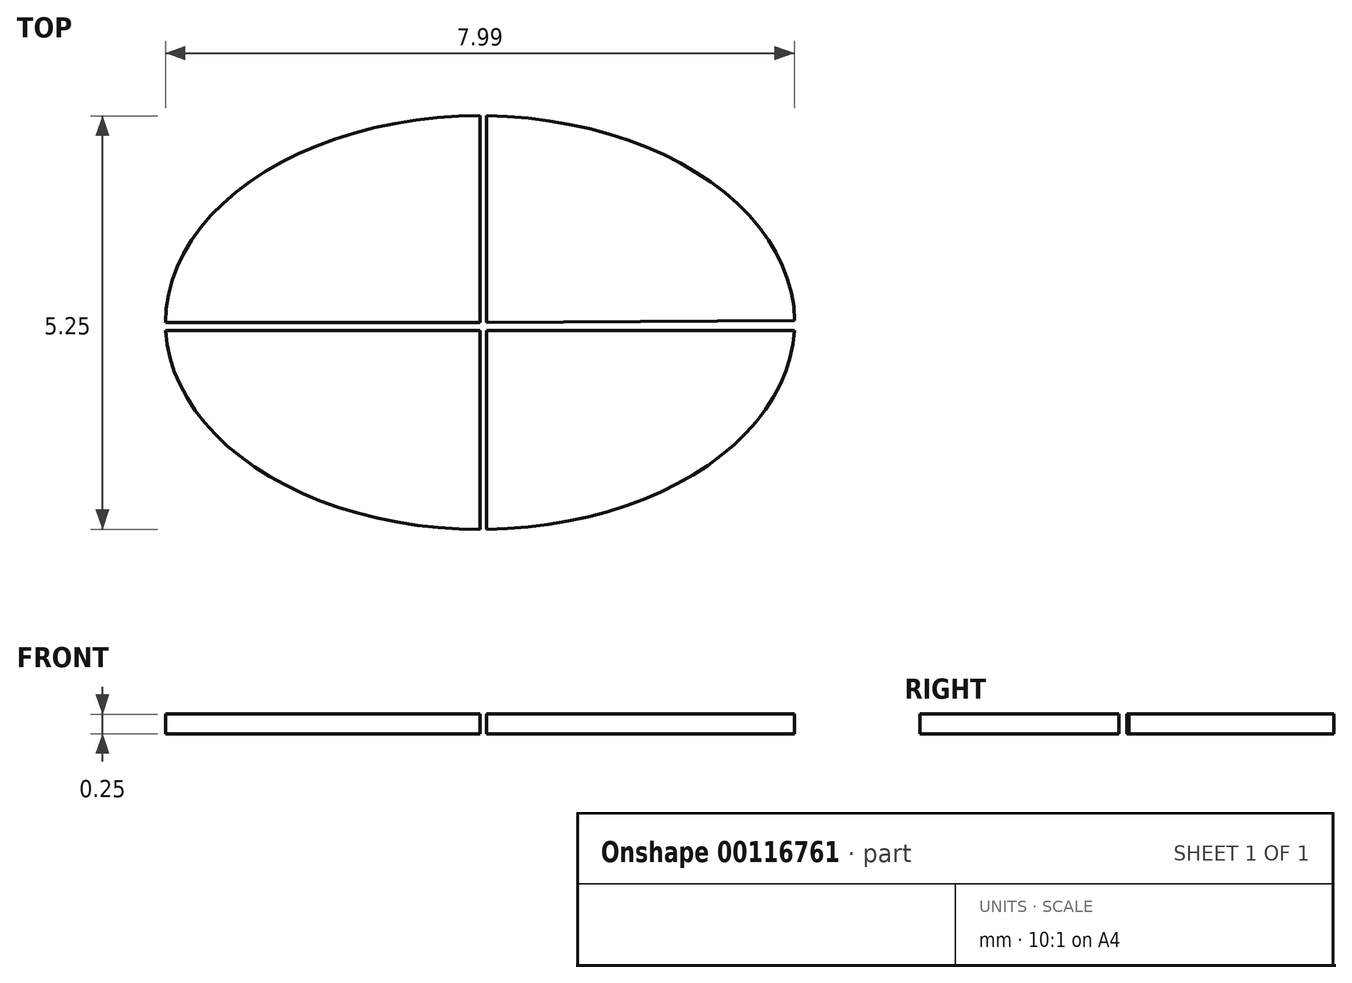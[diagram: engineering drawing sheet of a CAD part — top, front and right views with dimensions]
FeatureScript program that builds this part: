
annotation { "Feature Type Name" : "Feature", "Feature Type Description" : "" }
export const myFeature = defineFeature(function(context is Context, id is Id, definition is map)
    precondition{}
    {
        {
            var Q0;
            Q0=qCreatedBy(makeId("Top.planeOp"),FACE);
            var sketch = newSketch(context, id + "F0", { "sketchPlane" : qUnion([Q0])});
            skEllipticalArc(sketch, "E0", {});
            skLineSegment(sketch, "E1", {"start": v(-42.17, 8.75) * mm, "end": v(-42.17, 11.37) * mm});
            skLineSegment(sketch, "E2", {"start": v(-42.17, 12) * mm, "end": v(-42.09, 12) * mm});
            skLineSegment(sketch, "E3", {"start": v(-42.09, 12) * mm, "end": v(-42.09, 11.51) * mm});
            skLineSegment(sketch, "E4", {"start": v(-42.09, 5.27) * mm, "end": v(-42.17, 5.27) * mm});
            skLineSegment(sketch, "E5", {"start": v(-42.17, 5.27) * mm, "end": v(-42.17, 5.98) * mm});
            skLineSegment(sketch, "E6", {"start": v(-42.17, 8.75) * mm, "end": v(-46.17, 8.75) * mm});
            skLineSegment(sketch, "E7", {"start": v(-47.34, 8.75) * mm, "end": v(-46.3, 8.64) * mm});
            skLineSegment(sketch, "E8", {"start": v(-46.17, 8.64) * mm, "end": v(-42.17, 8.64) * mm});
            skLineSegment(sketch, "E9", {"start": v(-42.09, 8.75) * mm, "end": v(-38.18, 8.77) * mm});
            skLineSegment(sketch, "E10", {"start": v(-38.04, 8.64) * mm, "end": v(-36.9, 8.78) * mm});
            skLineSegment(sketch, "E11.trimOffspring", {"start": v(-42.09, 11.37) * mm, "end": v(-42.09, 8.75) * mm});
            skLineSegment(sketch, "E12.trimOffspring", {"start": v(-42.17, 11.51) * mm, "end": v(-42.17, 12) * mm});
            skLineSegment(sketch, "E13.trimOffspring", {"start": v(-42.09, 8.64) * mm, "end": v(-38.18, 8.64) * mm});
            skLineSegment(sketch, "E14.trimOffspring", {"start": v(-42.09, 8.64) * mm, "end": v(-42.09, 6.12) * mm});
            skEllipticalArc(sketch, "E15.trimOffspring", {});
            skLineSegment(sketch, "E16.trimOffspring", {"start": v(-38.04, 8.77) * mm, "end": v(-36.9, 8.78) * mm});
            skEllipticalArc(sketch, "E17.trimOffspring", {});
            skLineSegment(sketch, "E18.trimOffspring", {"start": v(-42.09, 5.98) * mm, "end": v(-42.09, 5.27) * mm});
            skLineSegment(sketch, "E19.trimOffspring", {"start": v(-42.17, 6.12) * mm, "end": v(-42.17, 8.64) * mm});
            skEllipticalArc(sketch, "E20.trimOffspring", {});
            skEllipticalArc(sketch, "E21.trimOffspring", {});
            skLineSegment(sketch, "E22.trimOffspring", {"start": v(-46.3, 8.75) * mm, "end": v(-47.34, 8.75) * mm});
            const initialGuessF0  = {"E0": [-0.04217269644141197, 0.008745238929242791, 1, 0, 0.004132768626864048, 0.002768394281422402, 1.5707963267948966, 3.141592653589793], "E0": [-0.04217269644141197, 0.008745238929242791, 1, 0, 0.003996420226951127, 0.0026272982057421812, 1.5707963267948966, 3.141592653589793], "E15.trimOffspring": [-0.04217269644141197, 0.008745238929242791, 1, 0, 0.003996420226951127, 0.0026272982057421812, 0.009922026542200093, 1.5496599618926992], "E15.trimOffspring": [-0.04217269644141197, 0.008745238929242791, 1, 0, 0.004132768626864048, 0.002768394281422402, 0.009744544502959572, 1.5503573921187657], "E17.trimOffspring": [-0.04217269644141197, 0.008745238929242791, 1, 0, 0.003996420226951127, 0.0026272982057421812, 4.733525345286887, 6.244820131681447], "E20.trimOffspring": [-0.04217269644141197, 0.008745238929242791, 1, 0, 0.004132768626864048, 0.002768394281422402, 4.73282791506082, 6.2467763679358255], "E21.trimOffspring": [-0.04217269644141197, 0.008745238929242791, 1, 0, 0.004132768626864048, 0.002768394281422402, 3.178001592833554, 4.71238898038469], "E21.trimOffspring": [-0.04217269644141197, 0.008745238929242791, 1, 0, 0.003996420226951127, 0.0026272982057421812, 3.179957829087932, 4.71238898038469]};
            skSetInitialGuess(sketch, initialGuessF0);
            skSolve(sketch);
        }
        {
            var Q0;
            Q0 = qSketchRegion(id + "F0", true);
            extrude(context, id + "F1", {"entities" : qUnion([Q0]), "depth" : 0.25 * mm});
        }
    });
